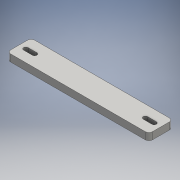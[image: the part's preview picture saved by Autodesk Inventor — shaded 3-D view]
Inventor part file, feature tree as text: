
AUTODESK INVENTOR PART (.ipt)
format: ipt  version: 2016 (Build 200138000, 138)  size: 109,056 bytes
history: native  units: mm
features: extrude x1, fillet x1, sketch x1
ambient origin geometry x8: Origin, YZ Plane, XZ Plane, XY Plane, X Axis, Y Axis, Z Axis, Center Point
bodies: Solid1 (feature_tree)
feature tree (3):
  extrude  "Extrusion1"  Depth=8.0mm TaperAngle=0.0deg
  fillet  "Fillet1"  Radius=4.0mm
  sketch  "Sketch1"  dims[d0=160.0mm d1=27.0mm d2=10.0mm d3=10.0mm d4=8.0mm d5=0.0mm d6=4.0mm]
